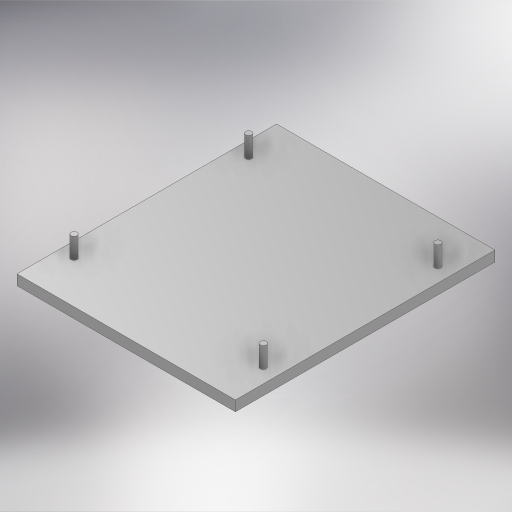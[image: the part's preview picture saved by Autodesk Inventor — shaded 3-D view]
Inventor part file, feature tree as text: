
AUTODESK INVENTOR PART (.ipt)
format: ipt  version: 2024 (Build 280153000, 153)  size: 338,432 bytes
history: native  units: mm
features: other x11, extrude x3, sketch x3
ambient origin geometry x8: Origin, YZ Plane, XZ Plane, XY Plane, X Axis, Y Axis, Z Axis, Center Point
bodies: Body1 (feature_tree)
feature tree (17):
  other  "Sólido1"
  extrude  "Extrusión1"  Depth=126.0mm
  extrude  "Extrusión2"  Depth=63.0mm
  extrude  "Extrusión3"  Depth=3.0mm
  sketch  "Boceto1"  dims[d1=106.0mm d2=126.0mm]
  sketch  "Boceto2"  dims[d3=53.0mm d4=63.0mm]
  sketch  "Boceto3"  dims[d5=5.0mm d6=0.0mm d7=3.0mm d8=20.616mm d9=7.071mm d10=10.0mm d11=0.0mm d12=52.5mm d13=126.0mm d14=106.0mm d15=52.5mm d16=35.0mm d17=35.0mm d18=35.0mm d19=35.0mm d20=35.0mm d21=2.0mm d22=0.0mm]
  other  "Finish1"
  other  "Finish2"
  other  "Finish3"
  other  "Finish4"
  other  "Finish5"
  other  "Finish6"
  other  "Finish7"
  other  "Finish8"
  other  "Finish9"
  other  "Finish10"
